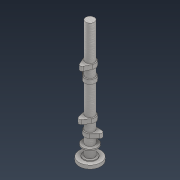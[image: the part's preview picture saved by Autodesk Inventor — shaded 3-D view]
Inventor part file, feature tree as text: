
AUTODESK INVENTOR PART (.ipt)
format: ipt  version: 2022 (Build 260153000, 153)  size: 215,552 bytes
history: native  units: mm
features: extrude x9, sketch x8, plane x7, fillet x2, hole x1
ambient origin geometry x8: Origin, YZ Plane, XZ Plane, XY Plane, X Axis, Y Axis, Z Axis, Center Point
bodies: Solid1 (feature_tree)
feature tree (27):
  extrude  "Extrusion1"  Depth=20.0mm
  plane  "Work Plane1"
  plane  "Work Plane2"
  plane  "Work Plane3"
  sketch  "Sketch2"  dims[d3=-101.515mm d4=15.0mm d5=-15.0mm d6=25.0mm]
  extrude  "Extrusion2"  Depth=25.0mm
  extrude  "Extrusion3"  Depth=10.0mm TaperAngle=0.0deg
  plane  "Work Plane4"
  plane  "Work Plane5"
  plane  "Work Plane6"
  fillet  "Fillet1"  Radius=25.0mm
  extrude  "Extrusion4"  Depth=10.0mm TaperAngle=0.0deg
  extrude  "Extrusion5"  Depth=15.0mm
  fillet  "Fillet2"  Radius=25.0mm
  sketch  "Sketch7"  dims[d22=1.745329mm d23=30.0mm]
  extrude  "Extrusion6"  Depth=30.0mm
  extrude  "Extrusion7"  Depth=25.0mm
  sketch  "Sketch8"  dims[d24=10.0mm d25=0.0mm d26=25.0mm]
  extrude  "Extrusion8"  Depth=30.0mm
  hole  "Hole1"  [1 undecoded]
  plane  "Work Plane7"
  extrude  "Extrusion9"  Depth=10.0mm TaperAngle=0.0deg
  sketch  "Sketch1"  dims[d0=283.0mm d1=0.0mm d2=20.0mm]
  sketch  "Sketch4"  dims[d7=30.0mm d8=10.0mm d9=0.0mm d10=25.0mm]
  sketch  "Sketch5"  dims[d12=30.0mm d13=10.0mm d14=0.0mm]
  sketch  "Sketch6"  dims[d15=5.0mm d16=-108.77mm d17=15.0mm d18=-15.0mm d19=43.633231mm d21=25.0mm]
  sketch  "Sketch9"  dims[d27=18.0mm d28=30.0mm d29=43.633231mm d30=10.0mm d31=0.0mm d32=5.0mm d33=30.0mm d34=50.0mm d35=8.0mm d36=0.0mm d37=10.0mm d38=0.0mm d39=30.0mm d41=360.0deg d43=40.0mm d44=5.0mm d45=30.0mm d46=5.0mm d47=0.0mm d48=10.0mm d49=4.134mm d50=5.0mm d51=4.0mm d52=2.0mm d53=90.0deg d54=5.0mm d55=0.0mm d56=21.76mm d57=35.0mm d58=3.0mm d59=0.0mm]
note: 1 required parameter value undecoded (feature->parameter linkage not recoverable at this tier; creation-order binding heuristic only, values carry confidence <= 0.55)
